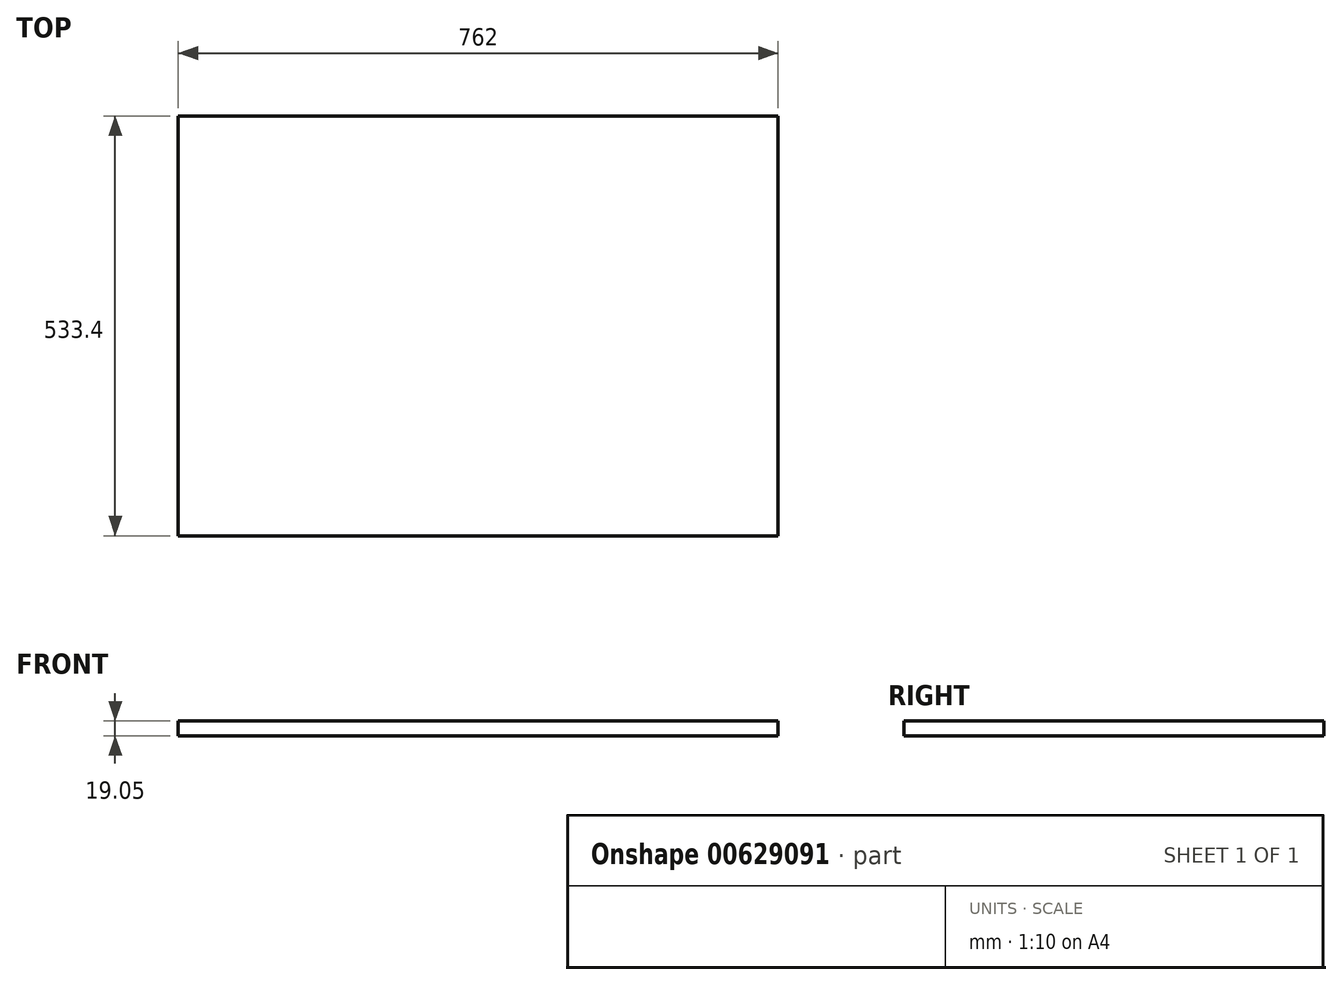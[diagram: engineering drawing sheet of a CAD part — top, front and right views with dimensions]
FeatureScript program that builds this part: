
annotation { "Feature Type Name" : "Feature", "Feature Type Description" : "" }
export const myFeature = defineFeature(function(context is Context, id is Id, definition is map)
    precondition{}
    {
        {
            var Q0;
            Q0=qCreatedBy(makeId("Top.planeOp"),FACE);
            var sketch = newSketch(context, id + "F0", { "sketchPlane" : qUnion([Q0])});
            skLineSegment(sketch, "E0.bottom", {"start": v(381, 266.7) * mm, "end": v(-381, 266.7) * mm});
            skLineSegment(sketch, "E0.top", {"start": v(381, -266.7) * mm, "end": v(-381, -266.7) * mm});
            skLineSegment(sketch, "E0.left", {"start": v(381, 266.7) * mm, "end": v(381, -266.7) * mm});
            skLineSegment(sketch, "E0.right", {"start": v(-381, 266.7) * mm, "end": v(-381, -266.7) * mm});
            skPoint(sketch, "E0.middle", {"position": v(0, 0) * mm});
            skSolve(sketch);
        }
        {
            var Q0;
            Q0=makeQuery(id+"F0.imprint","IMPRINT",FACE,{"disambiguationData":[TD([[makeQuery(id+"F0.imprint","IMPRINT",EDGE,{"derivedFrom":sQuery(id+"F0.wireOp",EDGE,"E0.bottom")}),1.0]])]});
            extrude(context, id + "F1", {"entities" : qUnion([Q0]), "depth" : 19.05 * mm, "offsetDistance" : 25.4 * mm});
        }
    });
